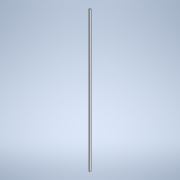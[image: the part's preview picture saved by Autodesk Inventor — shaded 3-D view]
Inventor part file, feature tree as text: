
AUTODESK INVENTOR PART (.ipt)
format: ipt  version: 2021 (Build 250183000, 183)  size: 93,696 bytes
history: native  units: mm
features: extrude x1, sketch x1
ambient origin geometry x8: Origin, YZ Plane, XZ Plane, XY Plane, X Axis, Y Axis, Z Axis, Center Point
bodies: Solid1 (feature_tree)
feature tree (2):
  extrude  "Extrusion1"  Depth=13.0mm
  sketch  "Sketch1"  dims[d0=13.0mm d1=13.0mm d2=1627.0mm d3=0.0mm]
